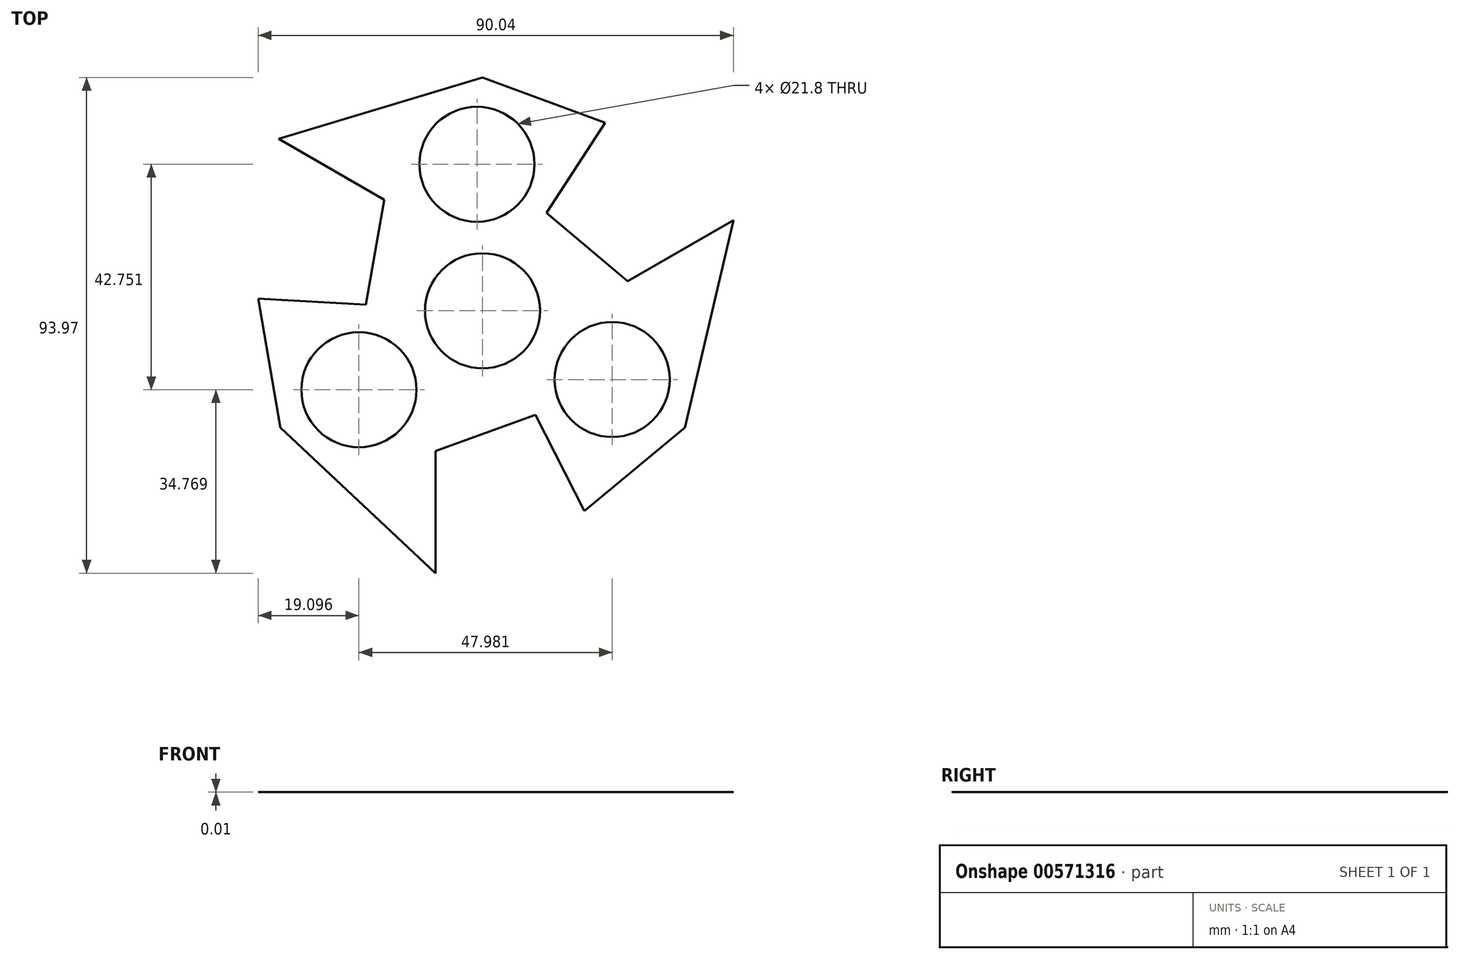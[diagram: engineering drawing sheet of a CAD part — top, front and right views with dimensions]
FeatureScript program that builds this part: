
annotation { "Feature Type Name" : "Feature", "Feature Type Description" : "" }
export const myFeature = defineFeature(function(context is Context, id is Id, definition is map)
    precondition{}
    {
        {
            var Q0;
            Q0=qCreatedBy(makeId("Top.planeOp"),FACE);
            var sketch = newSketch(context, id + "F0", { "sketchPlane" : qUnion([Q0])});
            skCircle(sketch, "E0", {"center": v(0, 0) * mm, "radius": 10.9 * mm});
            skCircle(sketch, "E1", {"center": v(-1.07, 27.78) * mm, "radius": 10.9 * mm});
            skCircle(sketch, "E2.1.0", {"center": v(-23.42, -14.97) * mm, "radius": 10.9 * mm});
            skCircle(sketch, "E2.2.0", {"center": v(24.56, -13.03) * mm, "radius": 10.9 * mm});
            skLineSegment(sketch, "E3", {"start": v(23.25, 35.67) * mm, "end": v(12.08, 18.54) * mm});
            skLineSegment(sketch, "E4", {"start": v(-38.62, 32.58) * mm, "end": v(-8.73, 41.6) * mm});
            skArc(sketch, "E5.trimOffspring", {"start": v(-25.2, 23.3) * mm, "mid": v(-25.2, 23.3) * mm, "end": v(-25.2, 23.3) * mm});
            skLineSegment(sketch, "E6", {"start": v(-22.1, 1.2) * mm, "end": v(-18.6, 21.01) * mm});
            skLineSegment(sketch, "E7.1.0", {"start": v(-42.52, 2.3) * mm, "end": v(-22.1, 1.2) * mm});
            skLineSegment(sketch, "E7.1.3", {"start": v(-33, -27.1) * mm, "end": v(-34.58, -25.61) * mm});
            skLineSegment(sketch, "E7.1.4", {"start": v(-8.9, -49.74) * mm, "end": v(-33, -27.1) * mm});
            skLineSegment(sketch, "E7.1.6", {"start": v(10.01, -19.73) * mm, "end": v(-8.9, -26.6) * mm});
            skLineSegment(sketch, "E7.2.0", {"start": v(19.26, -37.97) * mm, "end": v(10.01, -19.73) * mm});
            skLineSegment(sketch, "E7.2.3", {"start": v(39.97, -15.02) * mm, "end": v(39.47, -17.14) * mm});
            skLineSegment(sketch, "E7.2.4", {"start": v(47.52, 17.16) * mm, "end": v(39.97, -15.02) * mm});
            skLineSegment(sketch, "E7.2.6", {"start": v(12.08, 18.54) * mm, "end": v(27.5, 5.6) * mm});
            skLineSegment(sketch, "E8", {"start": v(-8.9, -26.6) * mm, "end": v(-8.9, -49.74) * mm});
            skLineSegment(sketch, "E9.1.0", {"start": v(27.5, 5.6) * mm, "end": v(47.52, 17.16) * mm});
            skLineSegment(sketch, "E9.2.0", {"start": v(-18.6, 21.01) * mm, "end": v(-38.62, 32.58) * mm});
            skLineSegment(sketch, "E10", {"start": v(-8.73, 41.6) * mm, "end": v(0, 44.23) * mm});
            skLineSegment(sketch, "E11", {"start": v(0, 44.23) * mm, "end": v(23.25, 35.67) * mm});
            skLineSegment(sketch, "E12.1.0", {"start": v(-38.3, -22.12) * mm, "end": v(-42.52, 2.3) * mm});
            skLineSegment(sketch, "E12.2.0", {"start": v(38.3, -22.12) * mm, "end": v(19.26, -37.97) * mm});
            skLineSegment(sketch, "E13.trimOffspring", {"start": v(-34.58, -25.61) * mm, "end": v(-38.3, -22.12) * mm});
            skLineSegment(sketch, "E14.trimOffspring", {"start": v(39.47, -17.14) * mm, "end": v(38.3, -22.12) * mm});
            skSolve(sketch);
        }
        {
            var Q0;
            Q0=qSketchRegion(id+"F0",true);
            extrude(context, id + "F1", {"entities" : qUnion([Q0]), "depth" : 1 / 101.6 * mm, "offsetDistance" : 25 * mm});
        }
    });
